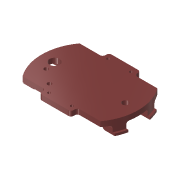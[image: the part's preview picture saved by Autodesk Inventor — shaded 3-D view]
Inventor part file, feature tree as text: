
AUTODESK INVENTOR PART (.ipt)
format: ipt  version: 2018 (Build 220112000, 112)  size: 267,776 bytes
history: native  units: mm
features: extrude x8, sketch x8, mirror x4, fillet x4
ambient origin geometry x8: Origin, YZ Plane, XZ Plane, XY Plane, X Axis, Y Axis, Z Axis, Center Point
bodies: Solid1 (feature_tree)
feature tree (24):
  extrude  "Extrusion1"  Depth=25.0mm
  extrude  "Extrusion2"  Depth=12.5mm
  mirror  "Mirror1"
  extrude  "Extrusion4"  Depth=4.0mm
  mirror  "Mirror2"
  extrude  "Extrusion6"  Depth=18.0mm
  extrude  "Extrusion7"  Depth=4.0mm
  mirror  "Mirror3"
  mirror  "Mirror4"
  fillet  "Fillet1"  Radius=4.2mm
  fillet  "Fillet2"  Radius=4.0mm
  fillet  "Fillet3"  Radius=76.2mm
  fillet  "Fillet4"  Radius=45.0mm
  extrude  "Extrusion8"  Depth=4.0mm TaperAngle=0.0deg
  extrude  "Extrusion9"  Depth=8.0mm
  extrude  "Extrusion10"  Depth=6.5mm TaperAngle=0.0deg
  sketch  "Sketch1"  dims[d0=55.0mm d1=25.0mm]
  sketch  "Sketch2"  dims[d2=27.5mm d3=12.5mm]
  sketch  "Sketch3"  dims[d4=4.0mm d5=0.0mm d6=2.3mm]
  sketch  "Sketch6"  dims[d7=2.3mm d8=18.0mm]
  sketch  "Sketch7"  dims[d9=9.0mm d10=4.2mm d11=4.2mm d12=4.0mm d13=0.0mm d14=76.2mm d15=45.0mm]
  sketch  "Sketch8"  dims[d16=22.5mm d19=4.0mm d20=0.0mm]
  sketch  "Sketch9"  dims[d29=8.0mm d30=6.0mm]
  sketch  "Sketch10"  dims[d31=8.0mm d32=6.5mm d33=0.0mm d34=79.375mm d35=1.75mm d36=0.0mm d37=2.0mm d38=2.0mm d39=2.0mm d40=2.0mm d42=3.302mm d43=15.0mm d44=17.0mm d45=3.302mm d46=8.89mm d47=11.43mm d48=10.0mm d49=0.0mm d50=4.85mm d51=27.94mm d52=10.0mm d53=0.0mm d54=6.5mm d55=10.0mm d56=0.0mm d62=8.0mm]
